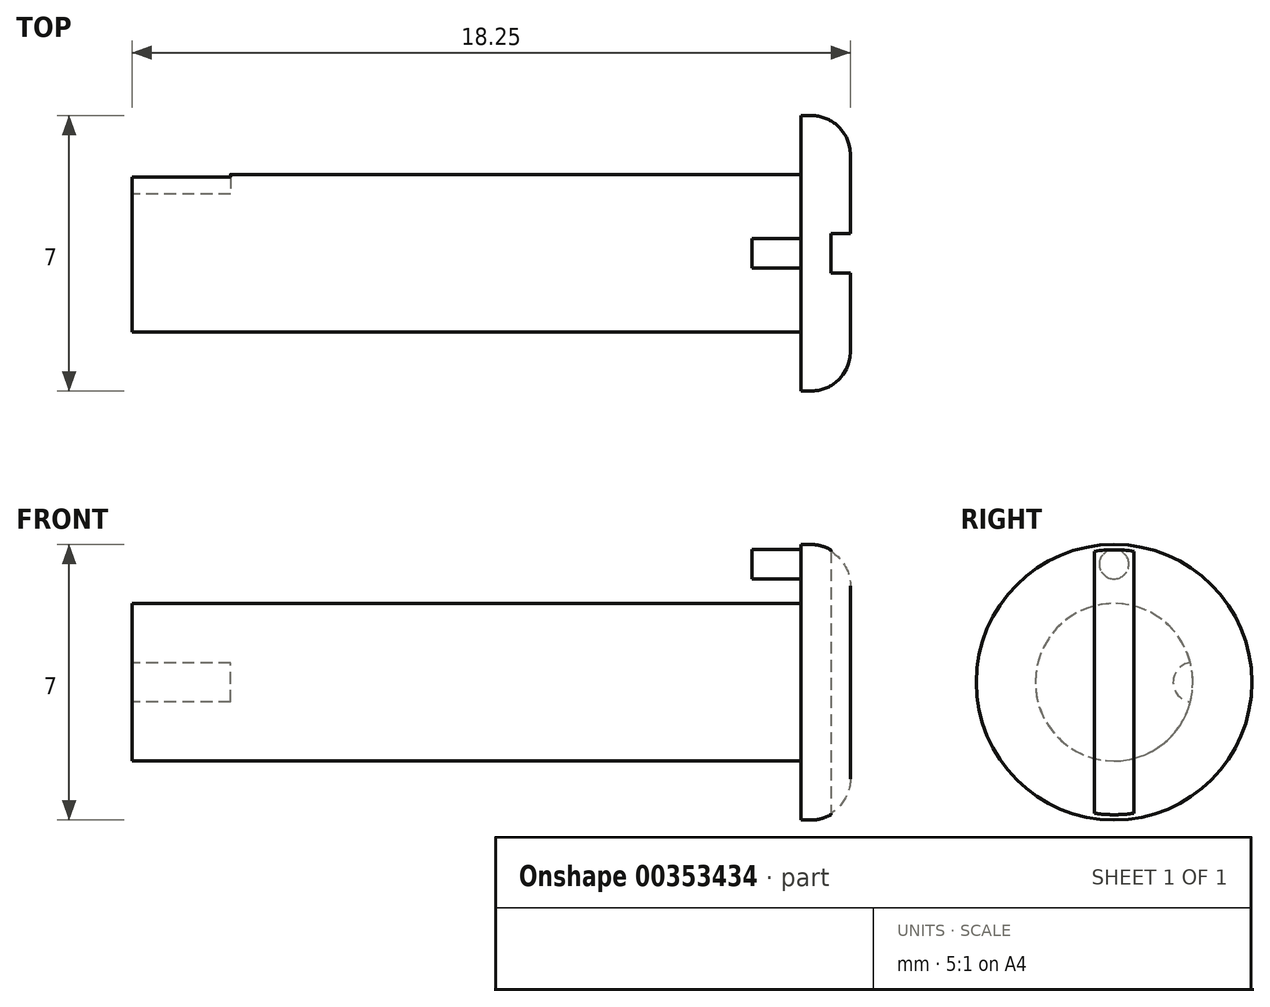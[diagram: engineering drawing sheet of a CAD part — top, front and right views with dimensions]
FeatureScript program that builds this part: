
annotation { "Feature Type Name" : "Feature", "Feature Type Description" : "" }
export const myFeature = defineFeature(function(context is Context, id is Id, definition is map)
    precondition{}
    {
        {
            var Q0;
            Q0=qCreatedBy(makeId("Right.planeOp"),FACE);
            var sketch = newSketch(context, id + "F0", { "sketchPlane" : qUnion([Q0])});
            skCircle(sketch, "E0", {"center": v(0, 0) * mm, "radius": 2 * mm});
            skSolve(sketch);
        }
        {
            var Q0;
            Q0=makeQuery(id+"F0.imprint","IMPRINT",FACE,{"disambiguationData":[TD([[makeQuery(id+"F0.imprint","IMPRINT",EDGE,{"derivedFrom":sQuery(id+"F0.wireOp",EDGE,"E0")}),1.0]])]});
            extrude(context, id + "F1", {"entities" : qUnion([Q0]), "oppositeDirection" : true, "depth" : 17 * mm});
        }
        {
            var Q0;
            Q0=makeQuery(id+"F1.opExtrude","CAP_FACE",FACE,{"disambiguationData":[OSD([sQuery(id+"F0.wireOp",EDGE,"E0")])],"isStart":true});
            var sketch = newSketch(context, id + "F2", { "sketchPlane" : qUnion([Q0])});
            skCircle(sketch, "E1", {"center": v(0, 0) * mm, "radius": 3.5 * mm});
            skSolve(sketch);
        }
        {
            var Q0;
            Q0 = qSketchRegion(id + "F2", true);
            extrude(context, id + "F3", {"entities" : qUnion([Q0]), "operationType" : NewBodyOperationType.ADD, "depth" : 1.25 * mm});
        }
        {
            var Q0;
            Q0=makeQuery(id+"F3.opExtrude","CAP_FACE",FACE,{"disambiguationData":[OSD([sQuery(id+"F2.wireOp",EDGE,"E1")])],"isStart":true});
            var sketch = newSketch(context, id + "F4", { "sketchPlane" : qUnion([Q0])});
            skCircle(sketch, "E2", {"center": v(0, 3) * mm, "radius": 0.38 * mm});
            skSolve(sketch);
        }
        {
            var Q0;
            Q0=makeQuery(id+"F4.imprint","IMPRINT",FACE,{"disambiguationData":[TD([[makeQuery(id+"F4.imprint","IMPRINT",EDGE,{"derivedFrom":sQuery(id+"F4.wireOp",EDGE,"E2")}),1.0]])]});
            extrude(context, id + "F5", {"entities" : qUnion([Q0]), "operationType" : NewBodyOperationType.ADD, "depth" : 1.25 * mm});
        }
        {
            var Q0;
            Q0=makeQuery(id+"F3.opExtrude","CAP_EDGE",EDGE,{"disambiguationData":[OSD([sQuery(id+"F2.wireOp",EDGE,"E1")])],"isStart":false});
            fillet(context, id + "F6", {"entities" : qUnion([Q0]), "radius" : 1 * mm, "tangentPropagation" : true, "allowEdgeOverflow" : false});
        }
        {
            var Q0;
            Q0=makeQuery(id+"F3.opExtrude","CAP_FACE",FACE,{"disambiguationData":[OSD([sQuery(id+"F2.wireOp",EDGE,"E1")])],"isStart":false});
            var sketch = newSketch(context, id + "F7", { "sketchPlane" : qUnion([Q0])});
            skLineSegment(sketch, "E3.bottom", {"start": v(0.5, 4.2) * mm, "end": v(-0.5, 4.2) * mm});
            skLineSegment(sketch, "E3.top", {"start": v(0.5, -4.2) * mm, "end": v(-0.5, -4.2) * mm});
            skLineSegment(sketch, "E3.left", {"start": v(0.5, 4.2) * mm, "end": v(0.5, -4.2) * mm});
            skLineSegment(sketch, "E3.right", {"start": v(-0.5, 4.2) * mm, "end": v(-0.5, -4.2) * mm});
            skPoint(sketch, "E3.middle", {"position": v(0, 0) * mm});
            skSolve(sketch);
        }
        {
            var Q0;
            Q0 = qSketchRegion(id + "F7", true);
            extrude(context, id + "F8", {"entities" : qUnion([Q0]), "operationType" : NewBodyOperationType.REMOVE, "oppositeDirection" : true, "depth" : .5 * mm});
        }
        {
            var Q0;
            Q0=makeQuery(id+"F1.opExtrude","CAP_FACE",FACE,{"disambiguationData":[OSD([sQuery(id+"F0.wireOp",EDGE,"E0")])],"isStart":false});
            var sketch = newSketch(context, id + "F9", { "sketchPlane" : qUnion([Q0])});
            skCircle(sketch, "E4.0", {"center": v(0, 0) * mm, "radius": 2 * mm});
            skArc(sketch, "E5", {"start": v(-1.94, -0.5) * mm, "mid": v(-1.5, 0) * mm, "end": v(-1.94, 0.5) * mm});
            skSolve(sketch);
        }
        {
            var Q0;
            {var subQ0=sQuery(id+"F9.wireOp",EDGE,"E5");Q0=makeQuery(id+"F9.imprint","IMPRINT",FACE,{"disambiguationData":[TD([[makeQuery(id+"F9.imprint","IMPRINT",EDGE,{"derivedFrom":subQ0}),1.0]])]});}
            extrude(context, id + "F10", {"entities" : qUnion([Q0]), "operationType" : NewBodyOperationType.REMOVE, "oppositeDirection" : true, "depth" : 2.5 * mm});
        }
    });
